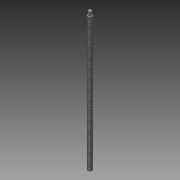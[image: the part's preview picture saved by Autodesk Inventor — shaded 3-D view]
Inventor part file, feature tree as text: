
AUTODESK INVENTOR PART (.ipt)
format: ipt  version: 2013 (Build 170138000, 138)  size: 75,776 bytes
history: native  units: in
note: dims shown in document units (in); Inventor stores cm internally (conversion verified against a paired STEP export)
features: extrude x2, sketch x2, thread x1
ambient origin geometry x8: Origin, YZ Plane, XZ Plane, XY Plane, X Axis, Y Axis, Z Axis, Center Point
bodies: Solid1 (feature_tree)
feature tree (5):
  extrude  "Extrusion1"  Depth=12.0in TaperAngle=0.0deg
  thread  "Thread1"  [1 undecoded]
  extrude  "Extrusion2"  Depth=0.105in
  sketch  "Sketch1"  dims[d0=0.375in d1=12.0in d2=0.0in d3=1.0in d4=0.0in]
  sketch  "Sketch2"  dims[d5=0.25in d6=0.105in d7=0.375in d8=0.0in]
note: 1 required parameter value undecoded (feature->parameter linkage not recoverable at this tier; creation-order binding heuristic only, values carry confidence <= 0.55)
